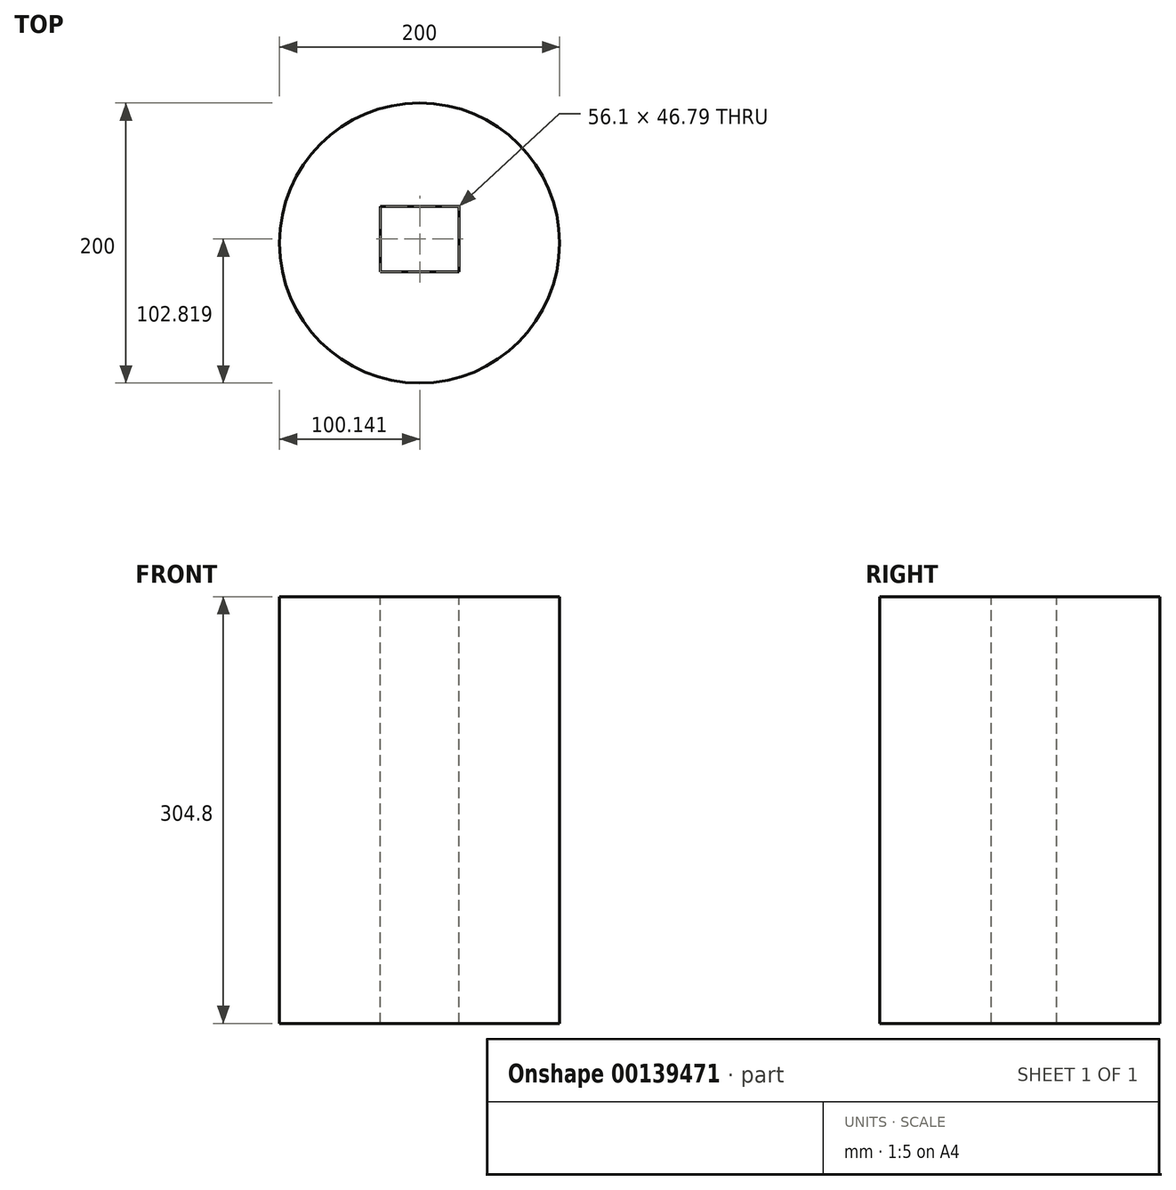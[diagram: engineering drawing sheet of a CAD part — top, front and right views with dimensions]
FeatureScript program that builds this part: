
annotation { "Feature Type Name" : "Feature", "Feature Type Description" : "" }
export const myFeature = defineFeature(function(context is Context, id is Id, definition is map)
    precondition{}
    {
        {
            var Q0;
            Q0=qCreatedBy(makeId("Top.planeOp"),FACE);
            var sketch = newSketch(context, id + "F0", { "sketchPlane" : qUnion([Q0])});
            skCircle(sketch, "E0", {"center": v(0, 0) * mm, "radius": 100 * mm});
            skSolve(sketch);
        }
        {
            var Q0;
            Q0 = qSketchRegion(id + "F0", true);
            extrude(context, id + "F1", {"entities" : qUnion([Q0]), "depth" : 304.8 * mm});
        }
        {
            var Q0;
            Q0=makeQuery(id+"F1.opExtrude","CAP_FACE",FACE,{"disambiguationData":[OSD([sQuery(id+"F0.wireOp",EDGE,"E0")])],"isStart":false});
            var sketch = newSketch(context, id + "F2", { "sketchPlane" : qUnion([Q0])});
            skLineSegment(sketch, "E1.bottom", {"start": v(-27.9, 26.22) * mm, "end": v(28.19, 26.22) * mm});
            skLineSegment(sketch, "E1.top", {"start": v(-27.9, -20.58) * mm, "end": v(28.19, -20.58) * mm});
            skLineSegment(sketch, "E1.left", {"start": v(-27.9, 26.22) * mm, "end": v(-27.9, -20.58) * mm});
            skLineSegment(sketch, "E1.right", {"start": v(28.19, 26.22) * mm, "end": v(28.19, -20.58) * mm});
            skSolve(sketch);
        }
        {
            var Q0;
            Q0 = qSketchRegion(id + "F2", true);
            extrude(context, id + "F3", {"entities" : qUnion([Q0]), "operationType" : NewBodyOperationType.REMOVE, "endBound" : BoundingType.THROUGH_ALL, "oppositeDirection" : true, "depth" : 25.4 * mm});
        }
    });
